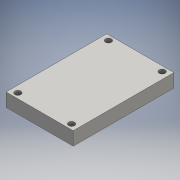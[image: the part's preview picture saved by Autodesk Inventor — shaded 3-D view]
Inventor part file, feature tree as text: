
AUTODESK INVENTOR PART (.ipt)
format: ipt  version: 2016 (Build 200138000, 138)  size: 103,424 bytes
history: native  units: mm
features: sketch x2, extrude x1, hole x1
ambient origin geometry x8: Origin, YZ Plane, XZ Plane, XY Plane, X Axis, Y Axis, Z Axis, Center Point
bodies: Solid1 (feature_tree)
feature tree (4):
  extrude  "Extrusion1"  Depth=75.0mm
  hole  "Hole1"  [1 undecoded]
  sketch  "Sketch1"  dims[d0=50.0mm d1=75.0mm]
  sketch  "Sketch2"  dims[d2=37.5mm d3=25.0mm d4=10.0mm d5=0.0mm d6=40.0mm d7=20.0mm d8=67.5mm d9=33.75mm d10=4.5mm d11=6.35mm d12=9.4mm d13=2.0mm d14=90.0deg d15=9.525mm d16=20.594885mm]
note: 1 required parameter value undecoded (feature->parameter linkage not recoverable at this tier; creation-order binding heuristic only, values carry confidence <= 0.55)
